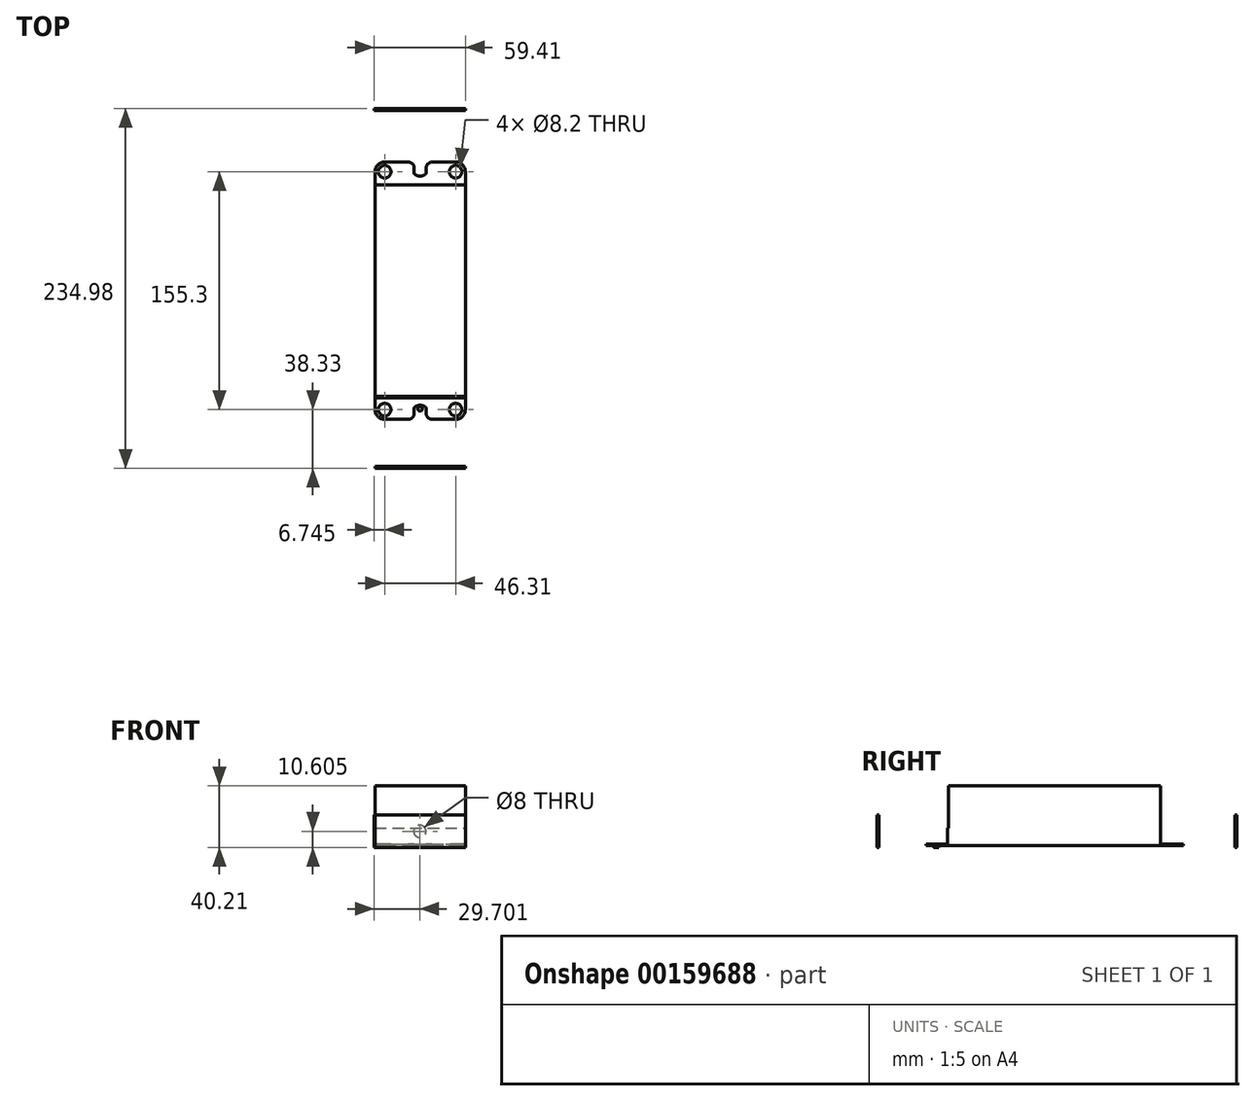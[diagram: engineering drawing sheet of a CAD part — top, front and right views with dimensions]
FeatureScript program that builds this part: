
annotation { "Feature Type Name" : "Feature", "Feature Type Description" : "" }
export const myFeature = defineFeature(function(context is Context, id is Id, definition is map)
    precondition{}
    {
        {
            var Q0;
            Q0=qCreatedBy(makeId("Top.planeOp"),FACE);
            var sketch = newSketch(context, id + "F0", { "sketchPlane" : qUnion([Q0])});
            skLineSegment(sketch, "E0.bottom", {"start": v(-23.15, 84) * mm, "end": v(-7.8, 84) * mm});
            skLineSegment(sketch, "E0.top", {"start": v(-23.16, -84) * mm, "end": v(-7.8, -84) * mm});
            skLineSegment(sketch, "E0.left", {"start": v(-29.5, 77.65) * mm, "end": v(-29.5, 72.96) * mm});
            skLineSegment(sketch, "E0.right", {"start": v(29.5, 77.65) * mm, "end": v(29.5, 72.96) * mm});
            skPoint(sketch, "E0.middle", {"position": v(0, 0) * mm});
            skPoint(sketch, "E1.visualSharp", {"position": v(-29.5, 84) * mm});
            skArc(sketch, "E1.filletArc", {"start": v(-23.15, 84) * mm, "mid": v(-27.65, 82.14) * mm, "end": v(-29.5, 77.65) * mm});
            skPoint(sketch, "E2.visualSharp", {"position": v(29.5, 84) * mm});
            skArc(sketch, "E2.filletArc", {"start": v(29.5, 77.65) * mm, "mid": v(27.65, 82.14) * mm, "end": v(23.16, 84) * mm});
            skPoint(sketch, "E3.visualSharp", {"position": v(29.5, -84) * mm});
            skArc(sketch, "E3.filletArc", {"start": v(23.16, -84) * mm, "mid": v(27.65, -82.14) * mm, "end": v(29.5, -77.65) * mm});
            skPoint(sketch, "E4.visualSharp", {"position": v(-29.5, -84) * mm});
            skArc(sketch, "E4.filletArc", {"start": v(-29.5, -77.65) * mm, "mid": v(-27.65, -82.14) * mm, "end": v(-23.16, -84) * mm});
            skCircle(sketch, "E5", {"center": v(-23.15, 77.65) * mm, "radius": 4.1 * mm});
            skCircle(sketch, "E6.MirrorC", {"center": v(23.15, 77.65) * mm, "radius": 4.1 * mm});
            skCircle(sketch, "E7.MirrorC", {"center": v(-23.15, -77.65) * mm, "radius": 4.1 * mm});
            skCircle(sketch, "E8.MirrorC", {"center": v(23.15, -77.65) * mm, "radius": 4.1 * mm});
            skLineSegment(sketch, "E9.bottom", {"start": v(-29.5, -72.96) * mm, "end": v(29.5, -72.96) * mm, "construction": true});
            skLineSegment(sketch, "E9.top", {"start": v(-29.5, 72.96) * mm, "end": v(29.5, 72.96) * mm, "construction": true});
            skLineSegment(sketch, "E9.left", {"start": v(-29.5, -72.96) * mm, "end": v(-29.5, 72.96) * mm});
            skLineSegment(sketch, "E9.right", {"start": v(29.5, -72.96) * mm, "end": v(29.5, 72.96) * mm});
            skArc(sketch, "E10", {"start": v(4, -76.51) * mm, "mid": v(0, -74.78) * mm, "end": v(-4, -76.51) * mm});
            skArc(sketch, "E11.MirrorC", {"start": v(4, 76.51) * mm, "mid": v(0, 74.78) * mm, "end": v(-4, 76.51) * mm});
            skLineSegment(sketch, "E12.trimOffspring", {"start": v(7.8, -84) * mm, "end": v(23.16, -84) * mm});
            skLineSegment(sketch, "E13", {"start": v(-4, -80.2) * mm, "end": v(-4, -76.51) * mm});
            skLineSegment(sketch, "E14", {"start": v(4, -80.2) * mm, "end": v(4, -76.51) * mm});
            skLineSegment(sketch, "E15.MirrorCS", {"start": v(-4, 80.2) * mm, "end": v(-4, 76.51) * mm});
            skLineSegment(sketch, "E16.MirrorCS", {"start": v(4, 80.2) * mm, "end": v(4, 76.51) * mm});
            skLineSegment(sketch, "E17.trimOffspring", {"start": v(7.8, 84) * mm, "end": v(23.16, 84) * mm});
            skPoint(sketch, "E18.visualSharp", {"position": v(-4, 84) * mm});
            skArc(sketch, "E18.filletArc", {"start": v(-4, 80.2) * mm, "mid": v(-5.11, 82.88) * mm, "end": v(-7.8, 84) * mm});
            skPoint(sketch, "E19.visualSharp", {"position": v(4, 84) * mm});
            skArc(sketch, "E19.filletArc", {"start": v(7.8, 84) * mm, "mid": v(5.11, 82.88) * mm, "end": v(4, 80.2) * mm});
            skPoint(sketch, "E20.visualSharp", {"position": v(-4, -84) * mm});
            skArc(sketch, "E20.filletArc", {"start": v(-7.8, -84) * mm, "mid": v(-5.11, -82.88) * mm, "end": v(-4, -80.2) * mm});
            skPoint(sketch, "E21.visualSharp", {"position": v(4, -84) * mm});
            skArc(sketch, "E21.filletArc", {"start": v(4, -80.2) * mm, "mid": v(5.11, -82.88) * mm, "end": v(7.8, -84) * mm});
            skLineSegment(sketch, "E22.trimOffspring", {"start": v(-29.5, -72.96) * mm, "end": v(-29.5, -77.65) * mm});
            skLineSegment(sketch, "E23.trimOffspring", {"start": v(29.5, -72.96) * mm, "end": v(29.5, -77.65) * mm});
            skSolve(sketch);
        }
        {
            var Q0;
            Q0 = qSketchRegion(id + "F0", true);
            extrude(context, id + "F1", {"entities" : qUnion([Q0]), "depth" : 1 * mm});
        }
        {
            var Q0;
            Q0=makeQuery(id+"F1.opExtrude","CAP_FACE",FACE,{"disambiguationData":[OSD([sQuery(id+"F0.wireOp",EDGE,"E0.bottom"),sQuery(id+"F0.wireOp",EDGE,"E0.top"),sQuery(id+"F0.wireOp",EDGE,"E0.left"),sQuery(id+"F0.wireOp",EDGE,"E0.right"),sQuery(id+"F0.wireOp",EDGE,"E1.filletArc"),sQuery(id+"F0.wireOp",EDGE,"E2.filletArc"),sQuery(id+"F0.wireOp",EDGE,"E3.filletArc"),sQuery(id+"F0.wireOp",EDGE,"E4.filletArc"),sQuery(id+"F0.wireOp",EDGE,"E5"),sQuery(id+"F0.wireOp",EDGE,"E6.MirrorC"),sQuery(id+"F0.wireOp",EDGE,"E7.MirrorC"),sQuery(id+"F0.wireOp",EDGE,"E8.MirrorC"),sQuery(id+"F0.wireOp",EDGE,"E9.left"),sQuery(id+"F0.wireOp",EDGE,"E9.right"),sQuery(id+"F0.wireOp",EDGE,"E10"),sQuery(id+"F0.wireOp",EDGE,"E11.MirrorC"),sQuery(id+"F0.wireOp",EDGE,"E12.trimOffspring"),sQuery(id+"F0.wireOp",EDGE,"E13"),sQuery(id+"F0.wireOp",EDGE,"E14"),sQuery(id+"F0.wireOp",EDGE,"E15.MirrorCS"),sQuery(id+"F0.wireOp",EDGE,"E16.MirrorCS"),sQuery(id+"F0.wireOp",EDGE,"E17.trimOffspring"),sQuery(id+"F0.wireOp",EDGE,"E18.filletArc"),sQuery(id+"F0.wireOp",EDGE,"E19.filletArc"),sQuery(id+"F0.wireOp",EDGE,"E20.filletArc"),sQuery(id+"F0.wireOp",EDGE,"E21.filletArc"),sQuery(id+"F0.wireOp",EDGE,"E22.trimOffspring"),sQuery(id+"F0.wireOp",EDGE,"E23.trimOffspring")])],"isStart":false});
            var sketch = newSketch(context, id + "F2", { "sketchPlane" : qUnion([Q0])});
            skLineSegment(sketch, "E24.bottom", {"start": v(-29.5, -69.15) * mm, "end": v(29.5, -69.15) * mm});
            skLineSegment(sketch, "E24.top", {"start": v(-29.5, 69.15) * mm, "end": v(29.5, 69.15) * mm});
            skLineSegment(sketch, "E24.left", {"start": v(-29.5, -69.15) * mm, "end": v(-29.5, 69.15) * mm});
            skLineSegment(sketch, "E24.right", {"start": v(29.5, -69.15) * mm, "end": v(29.5, 69.15) * mm});
            skPoint(sketch, "E24.middle", {"position": v(0, 0) * mm});
            skSolve(sketch);
        }
        {
            var Q0;
            Q0 = qSketchRegion(id + "F2", true);
            extrude(context, id + "F3", {"entities" : qUnion([Q0]), "operationType" : NewBodyOperationType.ADD, "depth" : 38 * mm});
        }
        {
            var Q0;
            Q0=makeQuery(id+"F1.opExtrude","CAP_FACE",FACE,{"disambiguationData":[OSD([sQuery(id+"F0.wireOp",EDGE,"E0.bottom"),sQuery(id+"F0.wireOp",EDGE,"E0.top"),sQuery(id+"F0.wireOp",EDGE,"E0.left"),sQuery(id+"F0.wireOp",EDGE,"E0.right"),sQuery(id+"F0.wireOp",EDGE,"E1.filletArc"),sQuery(id+"F0.wireOp",EDGE,"E2.filletArc"),sQuery(id+"F0.wireOp",EDGE,"E3.filletArc"),sQuery(id+"F0.wireOp",EDGE,"E4.filletArc"),sQuery(id+"F0.wireOp",EDGE,"E5"),sQuery(id+"F0.wireOp",EDGE,"E6.MirrorC"),sQuery(id+"F0.wireOp",EDGE,"E7.MirrorC"),sQuery(id+"F0.wireOp",EDGE,"E8.MirrorC"),sQuery(id+"F0.wireOp",EDGE,"E9.left"),sQuery(id+"F0.wireOp",EDGE,"E9.right"),sQuery(id+"F0.wireOp",EDGE,"E10"),sQuery(id+"F0.wireOp",EDGE,"E11.MirrorC"),sQuery(id+"F0.wireOp",EDGE,"E12.trimOffspring"),sQuery(id+"F0.wireOp",EDGE,"E13"),sQuery(id+"F0.wireOp",EDGE,"E14"),sQuery(id+"F0.wireOp",EDGE,"E15.MirrorCS"),sQuery(id+"F0.wireOp",EDGE,"E16.MirrorCS"),sQuery(id+"F0.wireOp",EDGE,"E17.trimOffspring"),sQuery(id+"F0.wireOp",EDGE,"E18.filletArc"),sQuery(id+"F0.wireOp",EDGE,"E19.filletArc"),sQuery(id+"F0.wireOp",EDGE,"E20.filletArc"),sQuery(id+"F0.wireOp",EDGE,"E21.filletArc"),sQuery(id+"F0.wireOp",EDGE,"E22.trimOffspring"),sQuery(id+"F0.wireOp",EDGE,"E23.trimOffspring")])],"isStart":true});
            var sketch = newSketch(context, id + "F4", { "sketchPlane" : qUnion([Q0])});
            skPoint(sketch, "E25.middle", {"position": v(0, 0) * mm});
            skLineSegment(sketch, "E26.MirrorCS", {"start": v(-29.48, 115.98) * mm, "end": v(29.5, 115.98) * mm});
            skPoint(sketch, "E27.MirrorCS.end.orphan", {"position": v(29.48, 98.68) * mm});
            skPoint(sketch, "E27.MirrorCS.start.orphan", {"position": v(-29.48, 75.98) * mm});
            skPoint(sketch, "E28.MirrorCS.end.orphan", {"position": v(29.5, 115.98) * mm});
            skPoint(sketch, "E29.top.start.orphan", {"position": v(-29.48, -115.98) * mm});
            skPoint(sketch, "E30.start.orphan", {"position": v(29.5, -87.55) * mm});
            skPoint(sketch, "E29.right.end.orphan", {"position": v(29.5, -115.98) * mm});
            skPoint(sketch, "E29.right.start.orphan", {"position": v(29.48, -98.68) * mm});
            skPoint(sketch, "E31.MirrorCS.end.orphan", {"position": v(-29.48, 115.98) * mm});
            skPoint(sketch, "E25.left.start.orphan", {"position": v(-29.5, 84) * mm});
            skPoint(sketch, "E32.start.orphan", {"position": v(-29.48, -75.98) * mm});
            skLineSegment(sketch, "E33", {"start": v(-29.48, 115.98) * mm, "end": v(-29.9, -118.41) * mm});
            skPoint(sketch, "E25.right.start.orphan", {"position": v(29.48, 75.98) * mm});
            skPoint(sketch, "E34.start.orphan", {"position": v(29.5, -84) * mm});
            skLineSegment(sketch, "E35", {"start": v(29.5, 115.98) * mm, "end": v(29.5, -119) * mm});
            skLineSegment(sketch, "E36", {"start": v(29.5, -119) * mm, "end": v(-29.9, -119) * mm});
            skLineSegment(sketch, "E37", {"start": v(-29.9, -119) * mm, "end": v(-29.9, -118.41) * mm});
            skSolve(sketch);
        }
        {
            var Q0;
            Q0 = qSketchRegion(id + "F4", true);
            extrude(context, id + "F5", {"entities" : qUnion([Q0]), "depth" : 1.21 * mm});
        }
        {
            var Q0;
            Q0=makeQuery(id+"F5.opExtrude","CAP_FACE",FACE,{"disambiguationData":[OSD([sQuery(id+"F4.wireOp",EDGE,"E26.MirrorCS"),sQuery(id+"F4.wireOp",EDGE,"uChj4hbl-qaNy-9vOZ-4t1b-X0IXo3OxWbXa"),sQuery(id+"F4.wireOp",EDGE,"E33"),sQuery(id+"F4.wireOp",EDGE,"E35")])],"isStart":true});
            var sketch = newSketch(context, id + "F6", { "sketchPlane" : qUnion([Q0])});
            skLineSegment(sketch, "E38.bottom", {"start": v(-29.48, -115.98) * mm, "end": v(29.5, -115.98) * mm});
            skLineSegment(sketch, "E38.top", {"start": v(-29.48, -114.77) * mm, "end": v(29.5, -114.77) * mm});
            skLineSegment(sketch, "E38.left", {"start": v(-29.48, -115.98) * mm, "end": v(-29.48, -114.77) * mm});
            skLineSegment(sketch, "E38.right", {"start": v(29.5, -115.98) * mm, "end": v(29.5, -114.77) * mm});
            skSolve(sketch);
        }
        {
            var Q0;
            Q0 = qSketchRegion(id + "F6", true);
            extrude(context, id + "F7", {"entities" : qUnion([Q0]), "operationType" : NewBodyOperationType.ADD, "depth" : 20 * mm});
        }
        {
            var Q0;
            Q0=makeQuery(id+"F5.opExtrude","CAP_FACE",FACE,{"disambiguationData":[OSD([sQuery(id+"F4.wireOp",EDGE,"E26.MirrorCS"),sQuery(id+"F4.wireOp",EDGE,"E33"),sQuery(id+"F4.wireOp",EDGE,"E35"),sQuery(id+"F4.wireOp",EDGE,"E36"),sQuery(id+"F4.wireOp",EDGE,"E37")])],"isStart":true});
            var sketch = newSketch(context, id + "F8", { "sketchPlane" : qUnion([Q0])});
            skLineSegment(sketch, "E39.bottom", {"start": v(-29.9, 119) * mm, "end": v(29.5, 119) * mm});
            skLineSegment(sketch, "E39.top", {"start": v(-29.9, 117.8) * mm, "end": v(29.5, 117.8) * mm});
            skLineSegment(sketch, "E39.left", {"start": v(-29.9, 119) * mm, "end": v(-29.9, 117.8) * mm});
            skLineSegment(sketch, "E39.right", {"start": v(29.5, 119) * mm, "end": v(29.5, 117.8) * mm});
            skSolve(sketch);
        }
        {
            var Q0;
            Q0 = qSketchRegion(id + "F8", true);
            extrude(context, id + "F9", {"entities" : qUnion([Q0]), "operationType" : NewBodyOperationType.ADD, "depth" : 20 * mm});
        }
        {
            var Q0;
            Q0=makeQuery(id+"F5.opExtrude","CAP_FACE",FACE,{"disambiguationData":[OSD([sQuery(id+"F4.wireOp",EDGE,"E26.MirrorCS"),sQuery(id+"F4.wireOp",EDGE,"E33"),sQuery(id+"F4.wireOp",EDGE,"E35"),sQuery(id+"F4.wireOp",EDGE,"E36"),sQuery(id+"F4.wireOp",EDGE,"E37")])],"isStart":true});
            var sketch = newSketch(context, id + "F10", { "sketchPlane" : qUnion([Q0])});
            skCircle(sketch, "E40", {"center": v(0, 77.19) * mm, "radius": 1.5 * mm});
            skCircle(sketch, "E41.MirrorC", {"center": v(0, -77.19) * mm, "radius": 1.5 * mm});
            skSolve(sketch);
        }
        {
            var Q0;
            Q0=makeQuery(id+"F10.imprint","IMPRINT",FACE,{"disambiguationData":[TD([[makeQuery(id+"F10.imprint","IMPRINT",EDGE,{"derivedFrom":sQuery(id+"F10.wireOp",EDGE,"E40")}),1.0]])]});
            var Q1;
            Q1=makeQuery(id+"F10.imprint","IMPRINT",FACE,{"disambiguationData":[TD([[makeQuery(id+"F10.imprint","IMPRINT",EDGE,{"derivedFrom":sQuery(id+"F10.wireOp",EDGE,"E41.MirrorC")}),-1.0]])]});
            extrude(context, id + "F11", {"entities" : qUnion([Q0, Q1]), "operationType" : NewBodyOperationType.REMOVE, "endBound" : BoundingType.UP_TO_NEXT, "oppositeDirection" : true, "depth" : 25 * mm});
        }
        {
            var Q0;
            Q0=makeQuery(id+"F9.boolean.opBoolean","MERGE",FACE,{"derivedFrom":[makeQuery(id+"F5.opExtrude","SWEPT_FACE",FACE,{"disambiguationData":[OSD([sQuery(id+"F4.wireOp",EDGE,"E36")])]}),makeQuery(id+"F9.opExtrude","SWEPT_FACE",FACE,{"disambiguationData":[OSD([sQuery(id+"F8.wireOp",EDGE,"E39.bottom")])]})]});
            var sketch = newSketch(context, id + "F12", { "sketchPlane" : qUnion([Q0])});
            skCircle(sketch, "E42", {"center": v(0.2, 9.4) * mm, "radius": 4 * mm});
            skPoint(sketch, "E42.centerSnap0", {"position": v(29.9, 9.4) * mm});
            skPoint(sketch, "E42.centerSnap1", {"position": v(0.2, 20) * mm});
            skSolve(sketch);
        }
        {
            var Q0;
            Q0 = qSketchRegion(id + "F12", true);
            extrude(context, id + "F13", {"entities" : qUnion([Q0]), "operationType" : NewBodyOperationType.REMOVE, "endBound" : BoundingType.UP_TO_NEXT, "oppositeDirection" : true, "depth" : 25 * mm});
        }
        {
            var Q0;
            Q0=makeQuery(id+"F3.opExtrude","SWEPT_FACE",FACE,{"disambiguationData":[OSD([sQuery(id+"F2.wireOp",EDGE,"E24.bottom")])]});
            var sketch = newSketch(context, id + "F14", { "sketchPlane" : qUnion([Q0])});
            skLineSegment(sketch, "E43.bottom", {"start": v(-29.5, 1) * mm, "end": v(29.5, 1) * mm});
            skLineSegment(sketch, "E43.top", {"start": v(-29.5, 11.55) * mm, "end": v(29.5, 11.55) * mm});
            skLineSegment(sketch, "E43.left", {"start": v(-29.5, 1) * mm, "end": v(-29.5, 11.55) * mm});
            skLineSegment(sketch, "E43.right", {"start": v(29.5, 1) * mm, "end": v(29.5, 11.55) * mm});
            skSolve(sketch);
        }
        {
            var Q0;
            Q0 = qSketchRegion(id + "F14", true);
            extrude(context, id + "F15", {"entities" : qUnion([Q0]), "operationType" : NewBodyOperationType.ADD, "depth" : 0.85 * mm});
        }
    });
